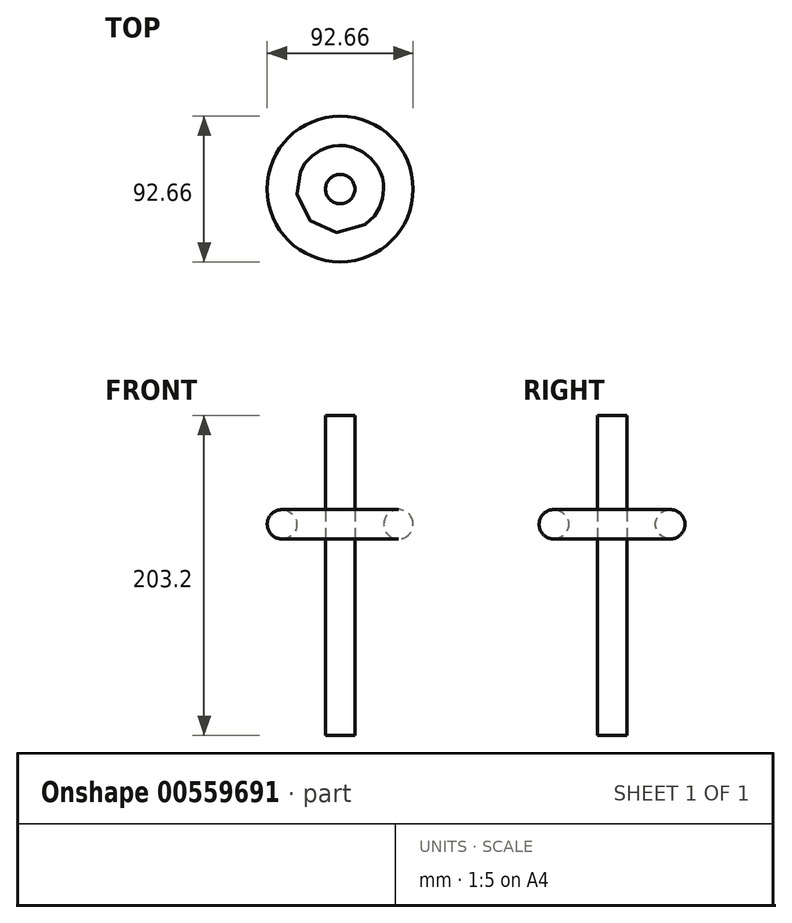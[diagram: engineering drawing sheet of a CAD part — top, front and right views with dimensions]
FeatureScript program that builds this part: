
annotation { "Feature Type Name" : "Feature", "Feature Type Description" : "" }
export const myFeature = defineFeature(function(context is Context, id is Id, definition is map)
    precondition{}
    {
        {
            var Q0;
            Q0=qCreatedBy(makeId("Front.planeOp"),FACE);
            var sketch = newSketch(context, id + "F0", { "sketchPlane" : qUnion([Q0])});
            skCircle(sketch, "E0", {"center": v(-37, 32.49) * mm, "radius": 9.33 * mm});
            skSolve(sketch);
        }
        {
            var Q0;
            Q0=qCreatedBy(makeId("Front.planeOp"),FACE);
            var sketch = newSketch(context, id + "F1", { "sketchPlane" : qUnion([Q0])});
            skLineSegment(sketch, "E1", {"start": v(0, 52.64) * mm, "end": v(0, -27.67) * mm});
            skSolve(sketch);
        }
        {
            var Q0;
            Q0 = qSketchRegion(id + "F0", true);
            var Q1;
            Q1=sQuery(id+"F1.wireOp",EDGE,"E1");
            revolve(context, id + "F2", {"entities" : qUnion([Q0]), "axis" : qUnion([Q1]), "revolveType" : RevolveType.ONE_DIRECTION, "angle" : 360 * degree});
        }
        {
            var Q0;
            Q0=qCreatedBy(makeId("Top.planeOp"),FACE);
            var sketch = newSketch(context, id + "F3", { "sketchPlane" : qUnion([Q0])});
            skCircle(sketch, "E2", {"center": v(0, 0) * mm, "radius": 9.33 * mm});
            skSolve(sketch);
        }
        {
            var Q0;
            Q0=makeQuery(id+"F3.imprint","IMPRINT",FACE,{"disambiguationData":[TD([[makeQuery(id+"F3.imprint","IMPRINT",EDGE,{"derivedFrom":sQuery(id+"F3.wireOp",EDGE,"E2")}),1.0]])]});
            extrude(context, id + "F4", {"entities" : qUnion([Q0]), "depth" : 101.6 * mm, "offsetDistance" : 25.4 * mm, "hasSecondDirection" : true, "secondDirectionOppositeDirection" : true, "secondDirectionDepth" : 101.6 * mm});
        }
        {
            var Q0;
            Q0=qCreatedBy(makeId("Front.planeOp"),FACE);
            var sketch = newSketch(context, id + "F5", { "sketchPlane" : qUnion([Q0])});
            skCircle(sketch, "E3", {"center": v(-55.95, -43.61) * mm, "radius": 11.15 * mm});
            skSolve(sketch);
        }
        {
            var Q0;
            Q0=sQuery(id+"F5.wireOp",EDGE,"E3");
            var Q1;
            Q1=makeQuery(id+"F4.opExtrude","SWEPT_FACE",FACE,{"disambiguationData":[OSD([sQuery(id+"F3.wireOp",EDGE,"E2")])]});
            revolve(context, id + "F6", {"bodyType" : ToolBodyType.SURFACE, "surfaceEntities" : qUnion([Q0]), "axis" : qUnion([Q1]), "revolveType" : RevolveType.FULL});
        }
    });
